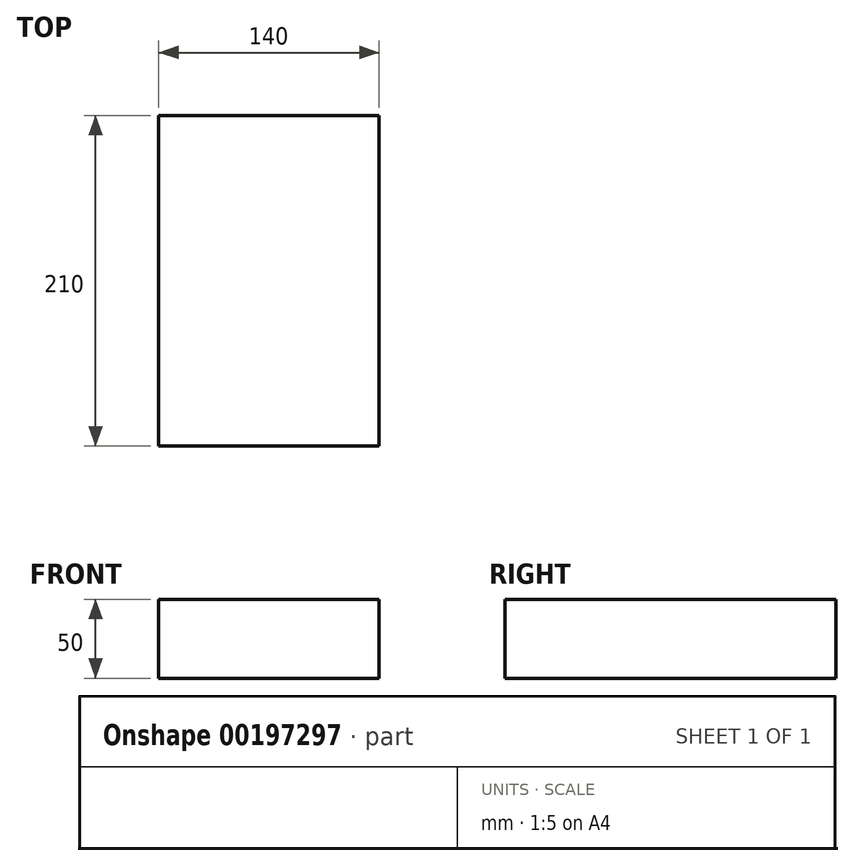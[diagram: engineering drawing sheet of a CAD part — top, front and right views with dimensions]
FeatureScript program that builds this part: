
annotation { "Feature Type Name" : "Feature", "Feature Type Description" : "" }
export const myFeature = defineFeature(function(context is Context, id is Id, definition is map)
    precondition{}
    {
        {
            var Q0;
            Q0=qCreatedBy(makeId("Top.planeOp"),FACE);
            var sketch = newSketch(context, id + "F0", { "sketchPlane" : qUnion([Q0])});
            skLineSegment(sketch, "E0.bottom", {"start": v(70, 105) * mm, "end": v(-70, 105) * mm});
            skLineSegment(sketch, "E0.top", {"start": v(70, -105) * mm, "end": v(-70, -105) * mm});
            skLineSegment(sketch, "E0.left", {"start": v(70, 105) * mm, "end": v(70, -105) * mm});
            skLineSegment(sketch, "E0.right", {"start": v(-70, 105) * mm, "end": v(-70, -105) * mm});
            skPoint(sketch, "E0.middle", {"position": v(0, 0) * mm});
            skCircle(sketch, "E1", {"center": v(-53, 90) * mm, "radius": 9.5 * mm});
            skCircle(sketch, "E2.0.1.0", {"center": v(-53, 61) * mm, "radius": 9.5 * mm});
            skCircle(sketch, "E2.0.2.0", {"center": v(-53, 32) * mm, "radius": 9.5 * mm});
            skCircle(sketch, "E2.0.3.0", {"center": v(-53, 3) * mm, "radius": 9.5 * mm});
            skCircle(sketch, "E2.1.0.0", {"center": v(-28, 90) * mm, "radius": 9.5 * mm});
            skCircle(sketch, "E2.1.1.0", {"center": v(-28, 61) * mm, "radius": 9.5 * mm});
            skCircle(sketch, "E2.1.2.0", {"center": v(-28, 32) * mm, "radius": 9.5 * mm});
            skCircle(sketch, "E2.1.3.0", {"center": v(-28, 3) * mm, "radius": 9.5 * mm});
            skLineSegment(sketch, "E2.direction1", {"start": v(-53, 90) * mm, "end": v(-28, 90) * mm, "construction": true});
            skLineSegment(sketch, "E2.direction2", {"start": v(-53, 90) * mm, "end": v(-53, 61) * mm, "construction": true});
            skSolve(sketch);
        }
        {
            var Q0;
            Q0=makeQuery(id+"F0.imprint","IMPRINT",FACE,{"disambiguationData":[TD([[makeQuery(id+"F0.imprint","IMPRINT",EDGE,{"derivedFrom":sQuery(id+"F0.wireOp",EDGE,"E0.bottom")}),1.0]])]});
            var Q1;
            Q1=makeQuery(id+"F0.imprint","IMPRINT",FACE,{"disambiguationData":[TD([[makeQuery(id+"F0.imprint","IMPRINT",EDGE,{"derivedFrom":sQuery(id+"F0.wireOp",EDGE,"E1")}),1.0]])]});
            var Q2;
            Q2=makeQuery(id+"F0.imprint","IMPRINT",FACE,{"disambiguationData":[TD([[makeQuery(id+"F0.imprint","IMPRINT",EDGE,{"derivedFrom":sQuery(id+"F0.wireOp",EDGE,"E2.1.0.0")}),1.0]])]});
            var Q3;
            Q3=makeQuery(id+"F0.imprint","IMPRINT",FACE,{"disambiguationData":[TD([[makeQuery(id+"F0.imprint","IMPRINT",EDGE,{"derivedFrom":sQuery(id+"F0.wireOp",EDGE,"E2.1.1.0")}),1.0]])]});
            var Q4;
            Q4=makeQuery(id+"F0.imprint","IMPRINT",FACE,{"disambiguationData":[TD([[makeQuery(id+"F0.imprint","IMPRINT",EDGE,{"derivedFrom":sQuery(id+"F0.wireOp",EDGE,"E2.0.1.0")}),1.0]])]});
            var Q5;
            Q5=makeQuery(id+"F0.imprint","IMPRINT",FACE,{"disambiguationData":[TD([[makeQuery(id+"F0.imprint","IMPRINT",EDGE,{"derivedFrom":sQuery(id+"F0.wireOp",EDGE,"E2.0.2.0")}),1.0]])]});
            var Q6;
            Q6=makeQuery(id+"F0.imprint","IMPRINT",FACE,{"disambiguationData":[TD([[makeQuery(id+"F0.imprint","IMPRINT",EDGE,{"derivedFrom":sQuery(id+"F0.wireOp",EDGE,"E2.1.2.0")}),1.0]])]});
            var Q7;
            Q7=makeQuery(id+"F0.imprint","IMPRINT",FACE,{"disambiguationData":[TD([[makeQuery(id+"F0.imprint","IMPRINT",EDGE,{"derivedFrom":sQuery(id+"F0.wireOp",EDGE,"E2.0.3.0")}),1.0]])]});
            var Q8;
            Q8=makeQuery(id+"F0.imprint","IMPRINT",FACE,{"disambiguationData":[TD([[makeQuery(id+"F0.imprint","IMPRINT",EDGE,{"derivedFrom":sQuery(id+"F0.wireOp",EDGE,"E2.1.3.0")}),1.0]])]});
            extrude(context, id + "F1", {"entities" : qUnion([Q0, Q1, Q2, Q3, Q4, Q5, Q6, Q7, Q8]), "depth" : 50 * mm});
        }
        {
            var Q0;
            Q0=makeQuery(id+"F1.opExtrude","CAP_FACE",FACE,{"disambiguationData":[OSD([sQuery(id+"F0.wireOp",EDGE,"E0.bottom"),sQuery(id+"F0.wireOp",EDGE,"E0.top"),sQuery(id+"F0.wireOp",EDGE,"E0.left"),sQuery(id+"F0.wireOp",EDGE,"E0.right")])],"isStart":false});
            var sketch = newSketch(context, id + "F2", { "sketchPlane" : qUnion([Q0])});
            skCircle(sketch, "E3", {"center": v(-25.26, 41.66) * mm, "radius": 26.5 * mm});
            skSolve(sketch);
        }
    });
